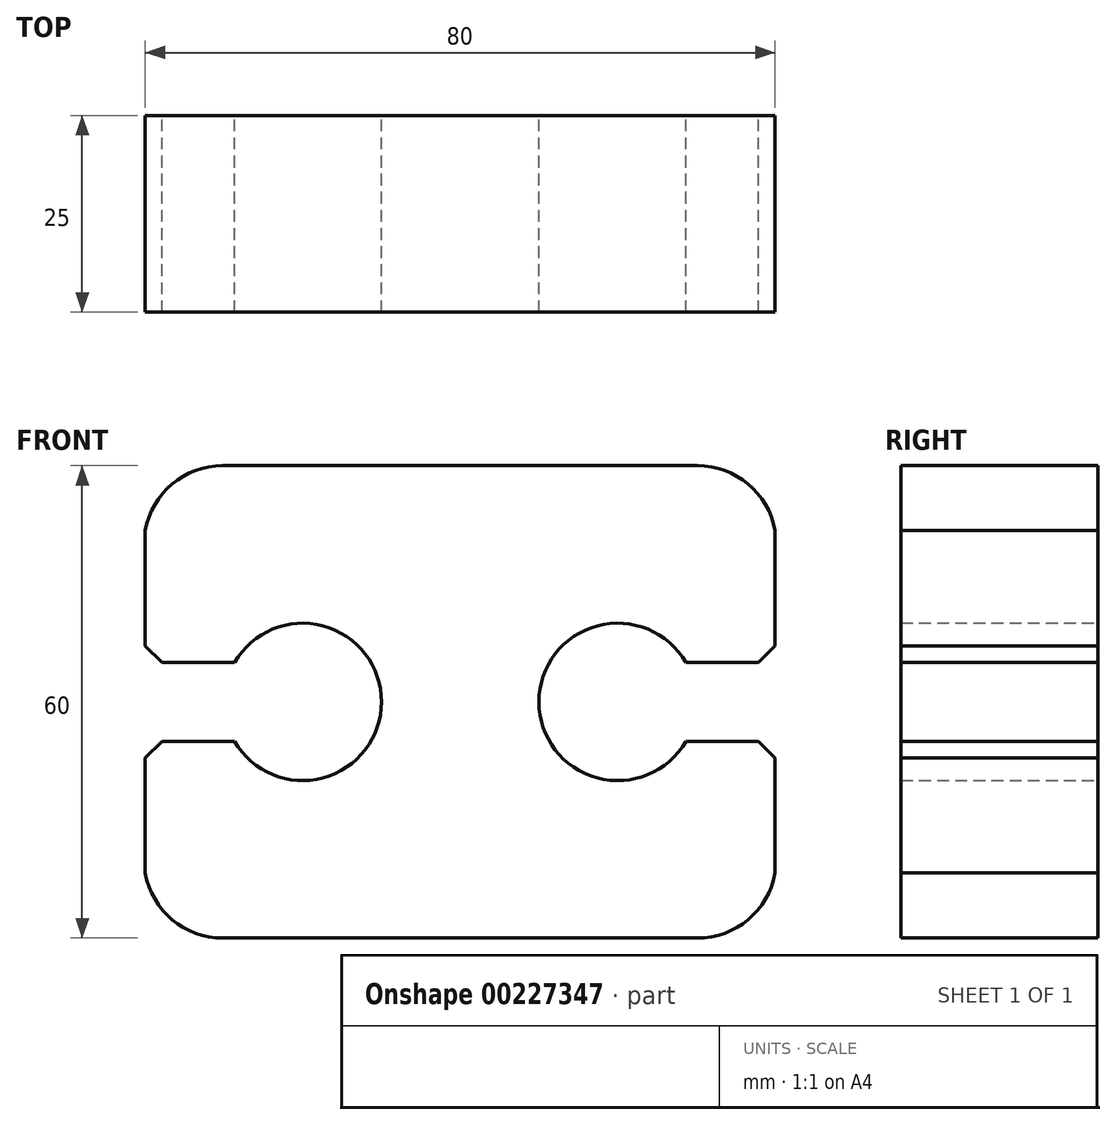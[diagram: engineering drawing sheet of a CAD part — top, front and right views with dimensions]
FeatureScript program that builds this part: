
annotation { "Feature Type Name" : "Feature", "Feature Type Description" : "" }
export const myFeature = defineFeature(function(context is Context, id is Id, definition is map)
    precondition{}
    {
        {
            var Q0;
            Q0=qCreatedBy(makeId("Front.planeOp"),FACE);
            var sketch = newSketch(context, id + "F0", { "sketchPlane" : qUnion([Q0])});
            skLineSegment(sketch, "E0", {"start": v(0, 30) * mm, "end": v(30.15, 30) * mm});
            skPoint(sketch, "E1.visualSharp", {"position": v(37.7, 30) * mm});
            skArc(sketch, "E1.filletArc", {"start": v(40, 21.75) * mm, "mid": v(36.58, 27.67) * mm, "end": v(30.15, 30) * mm});
            skLineSegment(sketch, "E2", {"start": v(40, 21.75) * mm, "end": v(40, 7.12) * mm});
            skLineSegment(sketch, "E3", {"start": v(37.88, 5) * mm, "end": v(28.66, 5) * mm});
            skLineSegment(sketch, "E4", {"start": v(37.88, 5) * mm, "end": v(40, 7.12) * mm});
            skLineSegment(sketch, "E5.MirrorCS", {"start": v(37.88, -5) * mm, "end": v(28.66, -5) * mm});
            skLineSegment(sketch, "E6.MirrorCS", {"start": v(37.88, -5) * mm, "end": v(40, -7.12) * mm});
            skLineSegment(sketch, "E7.MirrorCS", {"start": v(40, -21.75) * mm, "end": v(40, -7.12) * mm});
            skArc(sketch, "E8.MirrorCS", {"start": v(40, -21.75) * mm, "mid": v(36.58, -27.67) * mm, "end": v(30.15, -30) * mm});
            skLineSegment(sketch, "E9.MirrorCS", {"start": v(0, -30) * mm, "end": v(30.15, -30) * mm});
            skArc(sketch, "E10", {"start": v(28.66, 5) * mm, "mid": v(10, 0) * mm, "end": v(28.66, -5) * mm});
            skLineSegment(sketch, "E11.MirrorCS", {"start": v(0, 30) * mm, "end": v(-30.15, 30) * mm});
            skArc(sketch, "E12.MirrorCS", {"start": v(-40, 21.75) * mm, "mid": v(-36.58, 27.67) * mm, "end": v(-30.15, 30) * mm});
            skLineSegment(sketch, "E13.MirrorCS", {"start": v(-40, 21.75) * mm, "end": v(-40, 7.12) * mm});
            skLineSegment(sketch, "E14.MirrorCS", {"start": v(-37.88, 5) * mm, "end": v(-40, 7.12) * mm});
            skLineSegment(sketch, "E15.MirrorCS", {"start": v(-37.88, 5) * mm, "end": v(-28.66, 5) * mm});
            skArc(sketch, "E16.MirrorCS", {"start": v(-28.66, 5) * mm, "mid": v(-10, 0) * mm, "end": v(-28.66, -5) * mm});
            skLineSegment(sketch, "E17.MirrorCS", {"start": v(-37.88, -5) * mm, "end": v(-28.66, -5) * mm});
            skLineSegment(sketch, "E18.MirrorCS", {"start": v(-37.88, -5) * mm, "end": v(-40, -7.12) * mm});
            skLineSegment(sketch, "E19.MirrorCS", {"start": v(-40, -21.75) * mm, "end": v(-40, -7.12) * mm});
            skArc(sketch, "E20.MirrorCS", {"start": v(-40, -21.75) * mm, "mid": v(-36.58, -27.67) * mm, "end": v(-30.15, -30) * mm});
            skLineSegment(sketch, "E21.MirrorCS", {"start": v(0, -30) * mm, "end": v(-30.15, -30) * mm});
            skSolve(sketch);
        }
        {
            var Q0;
            Q0 = qSketchRegion(id + "F0", true);
            extrude(context, id + "F1", {"entities" : qUnion([Q0]), "depth" : 25 * mm});
        }
    });
